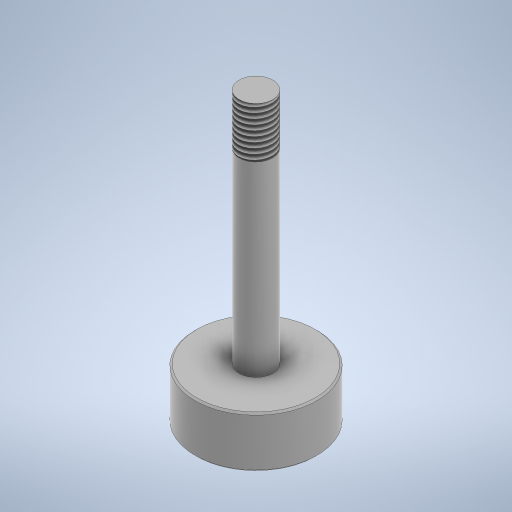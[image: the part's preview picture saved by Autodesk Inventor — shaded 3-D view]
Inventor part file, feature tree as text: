
AUTODESK INVENTOR PART (.ipt)
format: ipt  version: 2023 (Build 270158000, 158)  size: 275,968 bytes
history: native  units: mm
features: extrude x2, chamfer x2, sketch x2, other x1, thread x1
ambient origin geometry x8: Origin, YZ Plane, XZ Plane, XY Plane, X Axis, Y Axis, Z Axis, Center Point
bodies: Body1 (feature_tree)
feature tree (8):
  other  "Sólido1"
  extrude  "Extrusão1"  Depth=15.0mm TaperAngle=0.0deg
  extrude  "Extrusão2"  Depth=70.0mm TaperAngle=0.0deg
  thread  "Rosca1"  [1 undecoded]
  chamfer  "Chamfer1"  Distance=0.5mm Angle=45.0deg
  chamfer  "Chamfer2"  Distance=0.5mm Angle=45.0deg
  sketch  "Esboço1"  dims[d0=36.0mm d1=15.0mm d2=0.0mm]
  sketch  "Esboço2"  dims[d3=10.0mm d4=70.0mm d5=0.0mm d6=15.0mm d7=55.0mm d8=0.5mm d9=2.0mm d10=45.0deg d11=0.5mm d12=2.0mm d13=45.0deg]
note: 1 required parameter value undecoded (feature->parameter linkage not recoverable at this tier; creation-order binding heuristic only, values carry confidence <= 0.55)
